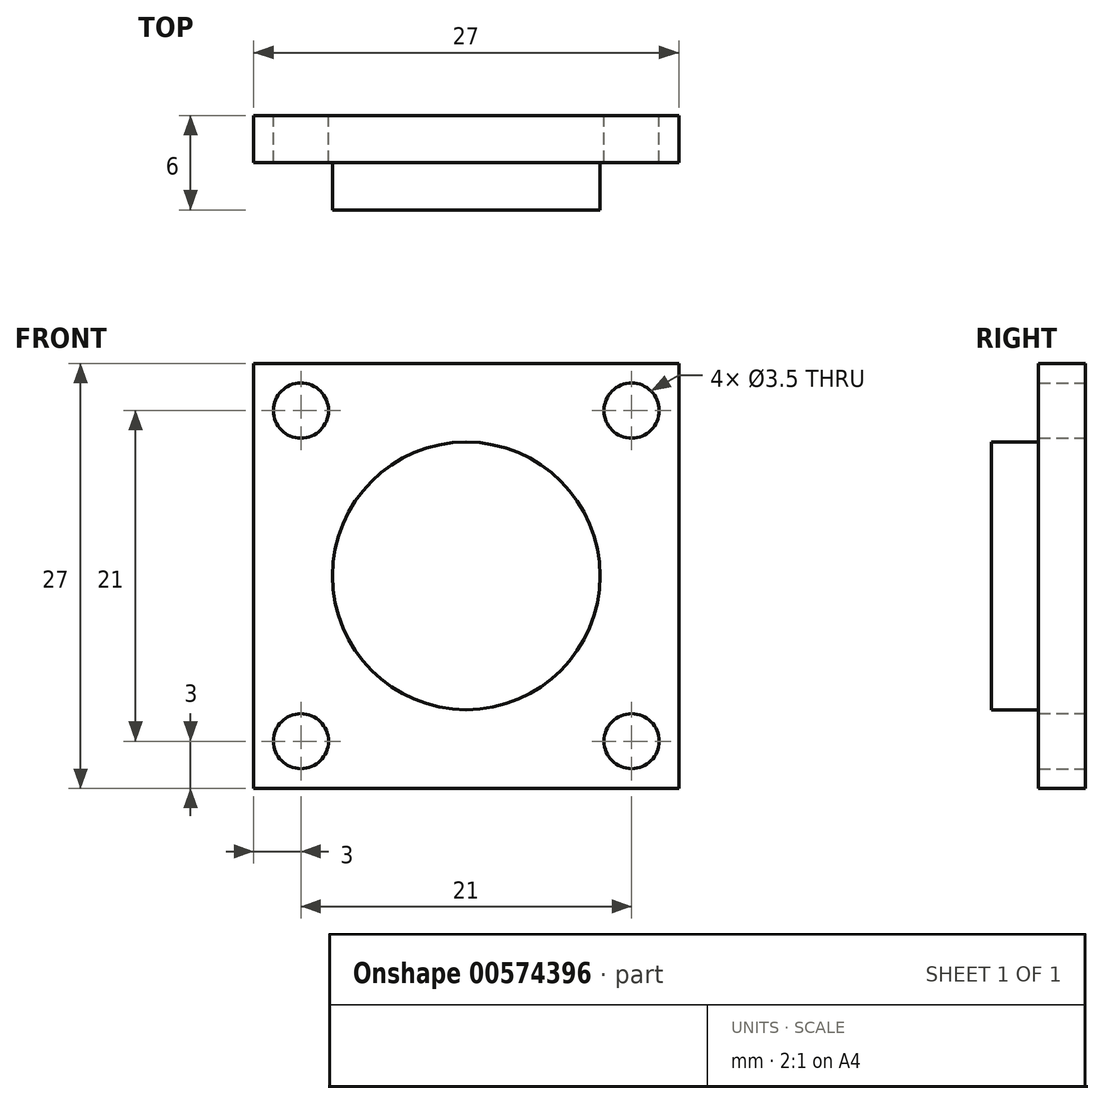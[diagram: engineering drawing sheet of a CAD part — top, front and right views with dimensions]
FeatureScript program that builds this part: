
annotation { "Feature Type Name" : "Feature", "Feature Type Description" : "" }
export const myFeature = defineFeature(function(context is Context, id is Id, definition is map)
    precondition{}
    {
        {
            var Q0;
            Q0=qCreatedBy(makeId("Front.planeOp"),FACE);
            var sketch = newSketch(context, id + "F0", { "sketchPlane" : qUnion([Q0])});
            skLineSegment(sketch, "E0.bottom", {"start": v(-13.5, 13.5) * mm, "end": v(13.5, 13.5) * mm});
            skLineSegment(sketch, "E0.top", {"start": v(-13.5, -13.5) * mm, "end": v(13.5, -13.5) * mm});
            skLineSegment(sketch, "E0.left", {"start": v(-13.5, 13.5) * mm, "end": v(-13.5, -13.5) * mm});
            skLineSegment(sketch, "E0.right", {"start": v(13.5, 13.5) * mm, "end": v(13.5, -13.5) * mm});
            skCircle(sketch, "E1", {"center": v(-10.5, 10.5) * mm, "radius": 1.75 * mm});
            skCircle(sketch, "E2.0.1.0", {"center": v(-10.5, -10.5) * mm, "radius": 1.75 * mm});
            skCircle(sketch, "E2.1.0.0", {"center": v(10.5, 10.5) * mm, "radius": 1.75 * mm});
            skCircle(sketch, "E2.1.1.0", {"center": v(10.5, -10.5) * mm, "radius": 1.75 * mm});
            skLineSegment(sketch, "E2.direction1", {"start": v(-10.5, 10.5) * mm, "end": v(10.5, 10.5) * mm, "construction": true});
            skLineSegment(sketch, "E2.direction2", {"start": v(-10.5, 10.5) * mm, "end": v(-10.5, -10.5) * mm, "construction": true});
            skSolve(sketch);
        }
        {
            var Q0;
            Q0=makeQuery(id+"F0.imprint","IMPRINT",FACE,{"disambiguationData":[TD([[makeQuery(id+"F0.imprint","IMPRINT",EDGE,{"derivedFrom":sQuery(id+"F0.wireOp",EDGE,"E0.bottom")}),-1.0]])]});
            extrude(context, id + "F1", {"entities" : qUnion([Q0]), "depth" : 3 * mm, "offsetDistance" : 25 * mm});
        }
        {
            var Q0;
            Q0=makeQuery(id+"F1.opExtrude","CAP_FACE",FACE,{"disambiguationData":[OSD([sQuery(id+"F0.wireOp",EDGE,"E0.bottom"),sQuery(id+"F0.wireOp",EDGE,"E0.top"),sQuery(id+"F0.wireOp",EDGE,"E0.left"),sQuery(id+"F0.wireOp",EDGE,"E0.right"),sQuery(id+"F0.wireOp",EDGE,"E1"),sQuery(id+"F0.wireOp",EDGE,"E2.0.1.0"),sQuery(id+"F0.wireOp",EDGE,"E2.1.0.0"),sQuery(id+"F0.wireOp",EDGE,"E2.1.1.0")])],"isStart":false});
            var sketch = newSketch(context, id + "F2", { "sketchPlane" : qUnion([Q0])});
            skCircle(sketch, "E3", {"center": v(0, 0) * mm, "radius": 8.5 * mm});
            skSolve(sketch);
        }
        {
            var Q0;
            Q0=makeQuery(id+"F2.imprint","IMPRINT",FACE,{"disambiguationData":[TD([[makeQuery(id+"F2.imprint","IMPRINT",EDGE,{"derivedFrom":sQuery(id+"F2.wireOp",EDGE,"E3")}),1.0]])]});
            extrude(context, id + "F3", {"entities" : qUnion([Q0]), "operationType" : NewBodyOperationType.ADD, "depth" : 3 * mm, "offsetDistance" : 25 * mm});
        }
    });
